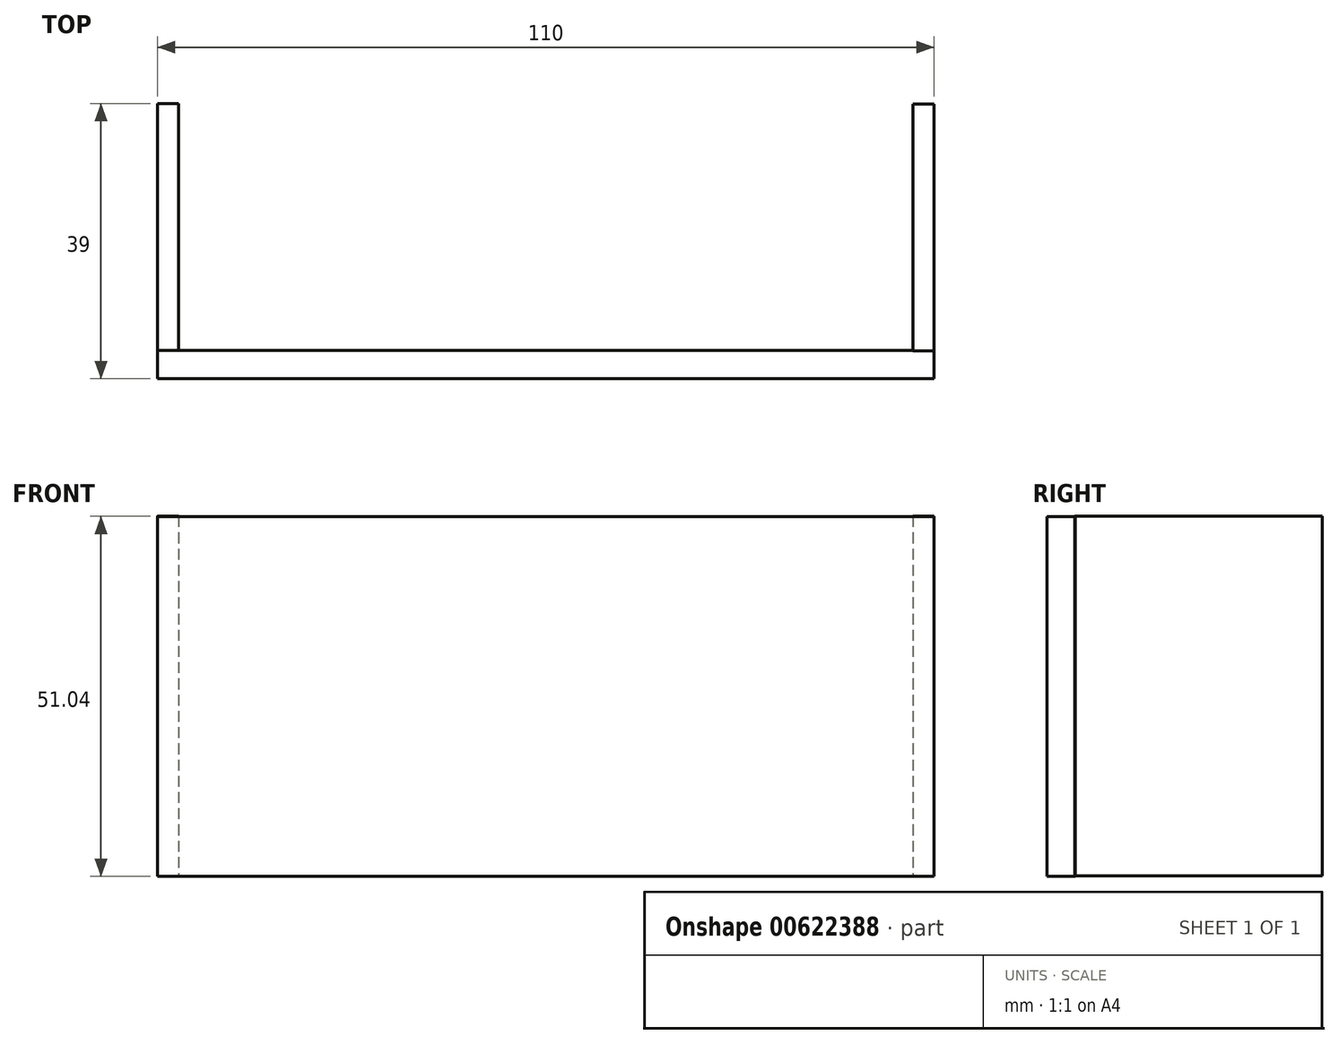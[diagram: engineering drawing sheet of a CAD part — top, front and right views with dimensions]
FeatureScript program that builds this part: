
annotation { "Feature Type Name" : "Feature", "Feature Type Description" : "" }
export const myFeature = defineFeature(function(context is Context, id is Id, definition is map)
    precondition{}
    {
        {
            var Q0;
            Q0=qCreatedBy(makeId("Front.planeOp"),FACE);
            var sketch = newSketch(context, id + "F0", { "sketchPlane" : qUnion([Q0])});
            skLineSegment(sketch, "E0.bottom", {"start": v(-55.2, 50.96) * mm, "end": v(54.8, 50.96) * mm});
            skLineSegment(sketch, "E0.top", {"start": v(-55.2, -0.04) * mm, "end": v(54.8, -0.04) * mm});
            skLineSegment(sketch, "E0.left", {"start": v(-55.2, 50.96) * mm, "end": v(-55.2, -0.04) * mm});
            skLineSegment(sketch, "E0.right", {"start": v(54.8, 50.96) * mm, "end": v(54.8, -0.04) * mm});
            skSolve(sketch);
        }
        {
            var Q0;
            Q0=makeQuery(id+"F0.imprint","IMPRINT",FACE,{"disambiguationData":[TD([[makeQuery(id+"F0.imprint","IMPRINT",EDGE,{"derivedFrom":sQuery(id+"F0.wireOp",EDGE,"E0.bottom")}),-1.0]])]});
            extrude(context, id + "F1", {"entities" : qUnion([Q0]), "depth" : 4 * mm, "offsetDistance" : 25 * mm});
        }
        {
            var Q0;
            Q0=qCreatedBy(makeId("Top.planeOp"),FACE);
            var sketch = newSketch(context, id + "F2", { "sketchPlane" : qUnion([Q0])});
            skLineSegment(sketch, "E1.bottom", {"start": v(-55.2, 0) * mm, "end": v(-52.2, 0) * mm});
            skLineSegment(sketch, "E1.top", {"start": v(-55.2, 35) * mm, "end": v(-52.2, 35) * mm});
            skLineSegment(sketch, "E1.left", {"start": v(-55.2, 0) * mm, "end": v(-55.2, 35) * mm});
            skLineSegment(sketch, "E1.right", {"start": v(-52.2, 0) * mm, "end": v(-52.2, 35) * mm});
            skSolve(sketch);
        }
        {
            var Q0;
            Q0 = qSketchRegion(id + "F2", true);
            extrude(context, id + "F3", {"entities" : qUnion([Q0]), "operationType" : NewBodyOperationType.ADD, "depth" : 51 * mm, "offsetDistance" : 25 * mm});
        }
        {
            var Q0;
            Q0=qCreatedBy(makeId("Top.planeOp"),FACE);
            var sketch = newSketch(context, id + "F4", { "sketchPlane" : qUnion([Q0])});
            skLineSegment(sketch, "E2.bottom", {"start": v(51.8, -0.05) * mm, "end": v(54.8, -0.05) * mm});
            skLineSegment(sketch, "E2.top", {"start": v(51.8, 34.95) * mm, "end": v(54.8, 34.95) * mm});
            skLineSegment(sketch, "E2.left", {"start": v(51.8, -0.05) * mm, "end": v(51.8, 34.95) * mm});
            skLineSegment(sketch, "E2.right", {"start": v(54.8, -0.05) * mm, "end": v(54.8, 34.95) * mm});
            skSolve(sketch);
        }
        {
            var Q0;
            Q0=makeQuery(id+"F4.imprint","IMPRINT",FACE,{"disambiguationData":[TD([[makeQuery(id+"F4.imprint","IMPRINT",EDGE,{"derivedFrom":sQuery(id+"F4.wireOp",EDGE,"E2.bottom")}),1.0]])]});
            extrude(context, id + "F5", {"entities" : qUnion([Q0]), "depth" : 51 * mm, "offsetDistance" : 25 * mm});
        }
    });
